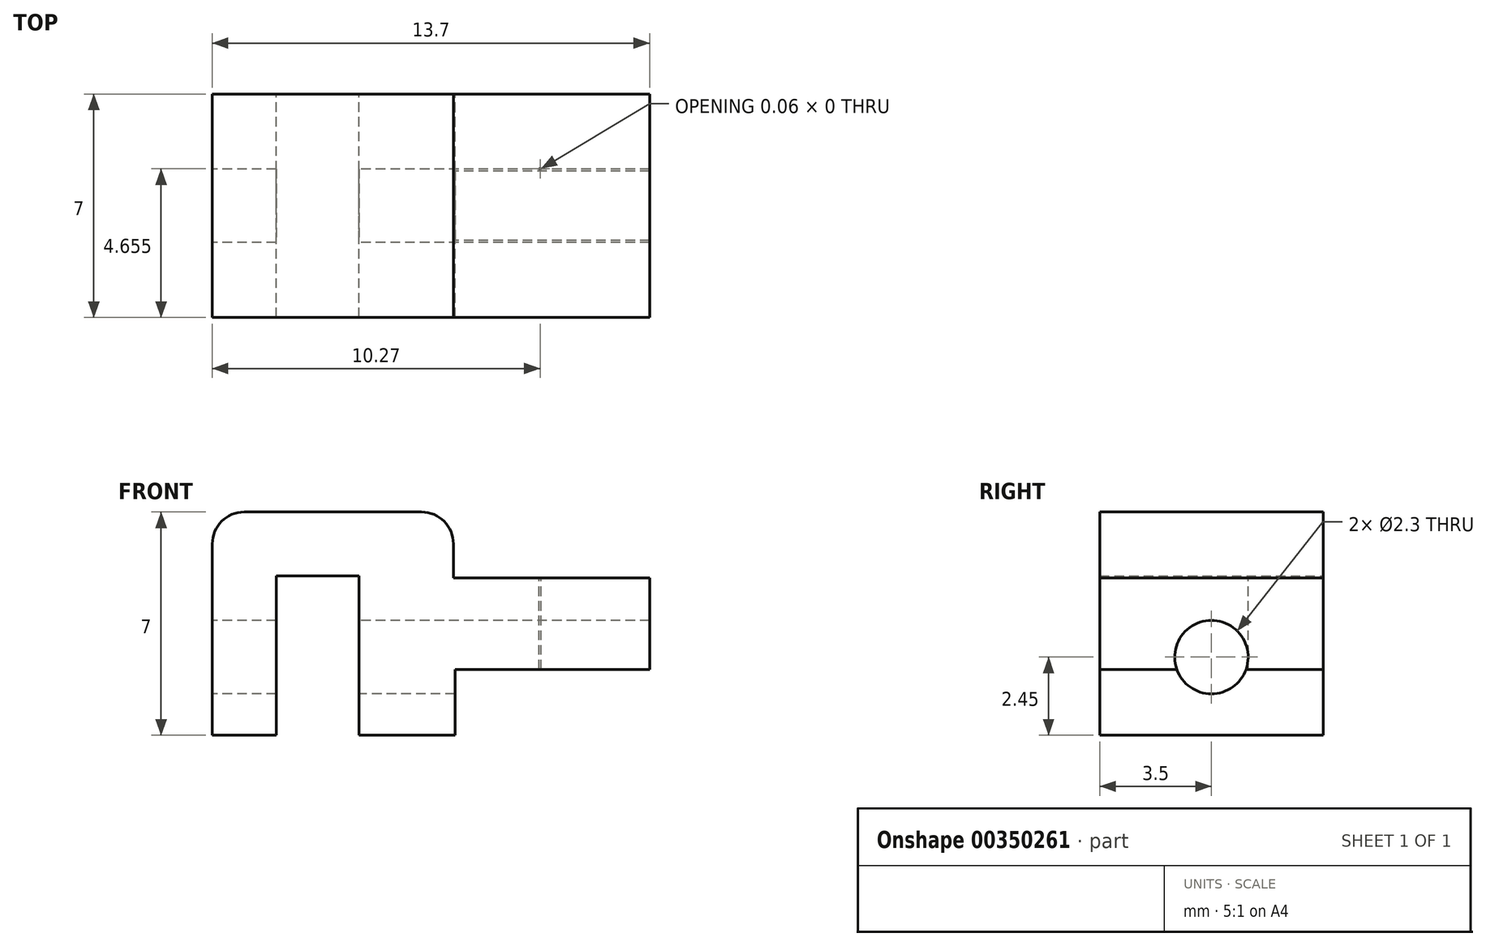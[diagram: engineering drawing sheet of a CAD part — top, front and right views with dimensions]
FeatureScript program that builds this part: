
annotation { "Feature Type Name" : "Feature", "Feature Type Description" : "" }
export const myFeature = defineFeature(function(context is Context, id is Id, definition is map)
    precondition{}
    {
        {
            var Q0;
            Q0=qCreatedBy(makeId("Front.planeOp"),FACE);
            var sketch = newSketch(context, id + "F0", { "sketchPlane" : qUnion([Q0])});
            skLineSegment(sketch, "E0.bottom", {"start": v(-2.84, 0) * mm, "end": v(-0.84, 0) * mm});
            skLineSegment(sketch, "E0.right", {"start": v(-0.84, 0) * mm, "end": v(-0.84, 5) * mm});
            skLineSegment(sketch, "E1", {"start": v(-0.84, 5) * mm, "end": v(1.76, 5) * mm});
            skLineSegment(sketch, "E2", {"start": v(1.76, 5) * mm, "end": v(1.76, 0) * mm});
            skLineSegment(sketch, "E3", {"start": v(1.76, 0) * mm, "end": v(4.76, 0) * mm});
            skLineSegment(sketch, "E4", {"start": v(4.76, 0) * mm, "end": v(4.76, 2.07) * mm});
            skLineSegment(sketch, "E5", {"start": v(4.76, 2.07) * mm, "end": v(10.86, 2.07) * mm});
            skLineSegment(sketch, "E6", {"start": v(10.86, 2.07) * mm, "end": v(10.86, 4.93) * mm});
            skLineSegment(sketch, "E7", {"start": v(3.71, 7) * mm, "end": v(-1.84, 7) * mm});
            skLineSegment(sketch, "E8", {"start": v(-2.84, 6) * mm, "end": v(-2.84, 0) * mm});
            skLineSegment(sketch, "E9", {"start": v(4.71, 6) * mm, "end": v(4.71, 4.93) * mm});
            skLineSegment(sketch, "E10", {"start": v(4.71, 4.93) * mm, "end": v(10.86, 4.93) * mm});
            skPoint(sketch, "E11.visualSharp", {"position": v(-2.84, 7) * mm});
            skArc(sketch, "E11.filletArc", {"start": v(-1.84, 7) * mm, "mid": v(-2.54, 6.7) * mm, "end": v(-2.84, 6) * mm});
            skPoint(sketch, "E12.visualSharp", {"position": v(4.71, 7) * mm});
            skArc(sketch, "E12.filletArc", {"start": v(4.71, 6) * mm, "mid": v(4.42, 6.7) * mm, "end": v(3.71, 7) * mm});
            skSolve(sketch);
        }
        {
            var Q0;
            Q0 = qSketchRegion(id + "F0", true);
            extrude(context, id + "F1", {"entities" : qUnion([Q0]), "endBound" : BoundingType.SYMMETRIC, "depth" : 7 * mm});
        }
        {
            var Q0;
            Q0=makeQuery(id+"F1.opExtrude","SWEPT_FACE",FACE,{"disambiguationData":[OSD([sQuery(id+"F0.wireOp",EDGE,"E8")])]});
            var sketch = newSketch(context, id + "F2", { "sketchPlane" : qUnion([Q0])});
            skCircle(sketch, "E13", {"center": v(0, 2.45) * mm, "radius": 1.15 * mm});
            skSolve(sketch);
        }
        {
            var Q0;
            Q0 = qSketchRegion(id + "F2", true);
            extrude(context, id + "F3", {"entities" : qUnion([Q0]), "operationType" : NewBodyOperationType.REMOVE, "oppositeDirection" : true, "depth" : 25 * mm});
        }
        {
            var Q0;
            Q0=makeQuery(id+"F1.opExtrude","SWEPT_FACE",FACE,{"disambiguationData":[OSD([sQuery(id+"F0.wireOp",EDGE,"E10")])]});
            var sketch = newSketch(context, id + "F4", { "sketchPlane" : qUnion([Q0])});
            skArc(sketch, "E14", {"start": v(7.46, 1.15) * mm, "mid": v(6.24, 0.03) * mm, "end": v(7.4, -1.16) * mm});
            skArc(sketch, "E15", {"start": v(9.33, -1.16) * mm, "mid": v(10.26, 0.06) * mm, "end": v(9.15, 1.1) * mm});
            skLineSegment(sketch, "E16", {"start": v(7.4, 1.16) * mm, "end": v(9.15, 1.1) * mm});
            skLineSegment(sketch, "E17", {"start": v(9.33, -1.16) * mm, "end": v(7.4, -1.16) * mm});
            skSolve(sketch);
        }
        {
            var Q0;
            {var subQ3=sQuery(id+"F4.wireOp",EDGE,"E14");Q0=makeQuery(id+"F4.imprint","IMPRINT",FACE,{"disambiguationData":[TD([[makeQuery(id+"F4.imprint","IMPRINT",EDGE,{"derivedFrom":subQ3}),1.0]])]});}
            extrude(context, id + "F5", {"entities" : qUnion([Q0]), "operationType" : NewBodyOperationType.REMOVE, "oppositeDirection" : true, "depth" : 25 * mm});
        }
    });
